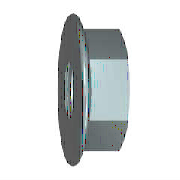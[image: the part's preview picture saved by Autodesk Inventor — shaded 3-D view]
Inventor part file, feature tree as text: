
AUTODESK INVENTOR PART (.ipt)
format: ipt  version: 2011 SP1 (Build 150282100, 282)  size: 195,584 bytes
history: native  units: mm (DEFAULTED — no unit token found)
features: other x2, chamfer x1, hole x1, plane x1
ambient origin geometry x7: Origin, YZ Plane, XZ Plane, X Axis, Y Axis, Z Axis, Center Point
bodies: Solid1 (feature_tree), Body (feature_tree)
feature tree (5):
  other  "Ring"
  chamfer  "Chamfer1"  Distance=11.8mm
  hole  "Thread"  [1 undecoded]
  other  "Work Axis1"
  plane  "Work Plane1"
note: 1 required parameter value undecoded (feature->parameter linkage not recoverable at this tier; creation-order binding heuristic only, values carry confidence <= 0.55)
